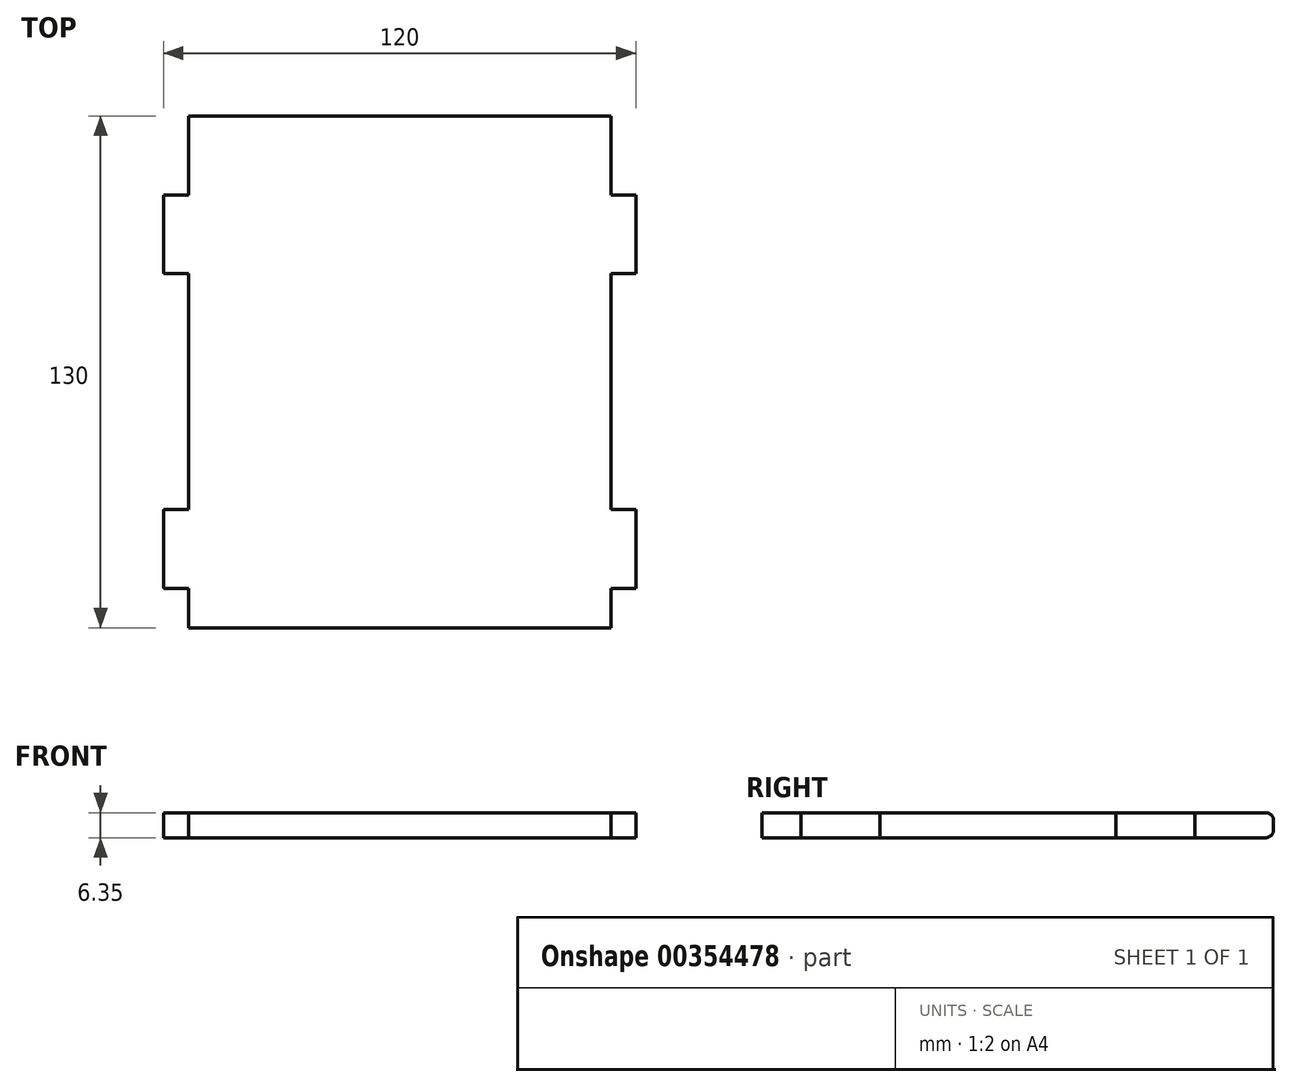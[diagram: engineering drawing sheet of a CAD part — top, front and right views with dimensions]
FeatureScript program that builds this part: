
annotation { "Feature Type Name" : "Feature", "Feature Type Description" : "" }
export const myFeature = defineFeature(function(context is Context, id is Id, definition is map)
    precondition{}
    {
        {
            var Q0;
            Q0=qCreatedBy(makeId("Top.planeOp"),FACE);
            var sketch = newSketch(context, id + "F0", { "sketchPlane" : qUnion([Q0])});
            skLineSegment(sketch, "E0.bottom", {"start": v(-117.05, 120) * mm, "end": v(-9.75, 120) * mm});
            skLineSegment(sketch, "E0.top", {"start": v(-117.05, -10) * mm, "end": v(-9.75, -10) * mm});
            skLineSegment(sketch, "E0.left", {"start": v(-117.05, 120) * mm, "end": v(-117.05, -10) * mm});
            skLineSegment(sketch, "E0.right", {"start": v(-9.75, 120) * mm, "end": v(-9.75, -10) * mm});
            skLineSegment(sketch, "E1.bottom", {"start": v(-123.4, 20) * mm, "end": v(-117.05, 20) * mm});
            skLineSegment(sketch, "E1.top", {"start": v(-123.4, 0) * mm, "end": v(-117.05, 0) * mm});
            skLineSegment(sketch, "E1.left", {"start": v(-123.4, 20) * mm, "end": v(-123.4, 0) * mm});
            skLineSegment(sketch, "E1.right", {"start": v(-117.05, 20) * mm, "end": v(-117.05, 0) * mm});
            skLineSegment(sketch, "E2.bottom", {"start": v(-123.4, 100) * mm, "end": v(-117.05, 100) * mm});
            skLineSegment(sketch, "E2.top", {"start": v(-123.4, 80) * mm, "end": v(-117.05, 80) * mm});
            skLineSegment(sketch, "E2.left", {"start": v(-123.4, 100) * mm, "end": v(-123.4, 80) * mm});
            skLineSegment(sketch, "E2.right", {"start": v(-117.05, 100) * mm, "end": v(-117.05, 80) * mm});
            skLineSegment(sketch, "E3.bottom", {"start": v(-9.75, 100) * mm, "end": v(-3.4, 100) * mm});
            skLineSegment(sketch, "E3.top", {"start": v(-9.75, 80) * mm, "end": v(-3.4, 80) * mm});
            skLineSegment(sketch, "E3.left", {"start": v(-9.75, 100) * mm, "end": v(-9.75, 80) * mm});
            skLineSegment(sketch, "E3.right", {"start": v(-3.4, 100) * mm, "end": v(-3.4, 80) * mm});
            skLineSegment(sketch, "E4.bottom", {"start": v(-9.75, 20) * mm, "end": v(-3.4, 20) * mm});
            skLineSegment(sketch, "E4.top", {"start": v(-9.75, 0) * mm, "end": v(-3.4, 0) * mm});
            skLineSegment(sketch, "E4.left", {"start": v(-9.75, 20) * mm, "end": v(-9.75, 0) * mm});
            skLineSegment(sketch, "E4.right", {"start": v(-3.4, 20) * mm, "end": v(-3.4, 0) * mm});
            skSolve(sketch);
        }
        {
            var Q0;
            {var subQ4=sQuery(id+"F0.wireOp",EDGE,"E0.bottom");Q0=makeQuery(id+"F0.imprint","IMPRINT",FACE,{"disambiguationData":[TD([[makeQuery(id+"F0.imprint","IMPRINT",EDGE,{"derivedFrom":subQ4}),-1.0]])]});}
            var Q1;
            Q1=makeQuery(id+"F0.imprint","IMPRINT",FACE,{"disambiguationData":[TD([[makeQuery(id+"F0.imprint","IMPRINT",EDGE,{"derivedFrom":sQuery(id+"F0.wireOp",EDGE,"E2.bottom")}),-1.0]])]});
            var Q2;
            Q2=makeQuery(id+"F0.imprint","IMPRINT",FACE,{"disambiguationData":[TD([[makeQuery(id+"F0.imprint","IMPRINT",EDGE,{"derivedFrom":sQuery(id+"F0.wireOp",EDGE,"E3.bottom")}),-1.0]])]});
            var Q3;
            Q3=makeQuery(id+"F0.imprint","IMPRINT",FACE,{"disambiguationData":[TD([[makeQuery(id+"F0.imprint","IMPRINT",EDGE,{"derivedFrom":sQuery(id+"F0.wireOp",EDGE,"E4.bottom")}),-1.0]])]});
            var Q4;
            Q4=makeQuery(id+"F0.imprint","IMPRINT",FACE,{"disambiguationData":[TD([[makeQuery(id+"F0.imprint","IMPRINT",EDGE,{"derivedFrom":sQuery(id+"F0.wireOp",EDGE,"E1.bottom")}),-1.0]])]});
            extrude(context, id + "F1", {"entities" : qUnion([Q0, Q1, Q2, Q3, Q4]), "depth" : 6.35 * mm});
        }
        {
            var Q0;
            Q0=makeQuery(id+"F1.opExtrude","CAP_EDGE",EDGE,{"disambiguationData":[OSD([sQuery(id+"F0.wireOp",EDGE,"E0.bottom")])],"isStart":false});
            var Q1;
            Q1=makeQuery(id+"F1.opExtrude","CAP_EDGE",EDGE,{"disambiguationData":[OSD([sQuery(id+"F0.wireOp",EDGE,"E0.bottom")])],"isStart":true});
            fillet(context, id + "F2", {"entities" : qUnion([Q0, Q1]), "radius" : 2 * mm, "tangentPropagation" : true, "allowEdgeOverflow" : false});
        }
    });
